# Revit family: Турникет тумбовый PERCo_TTD-03.2
name_source: partatom
category: Mechanical Equipment
units: mm (PartAtom-declared; Revit-internal decimal feet)

## family parameters
Always vertical = No
Classification = None
Cut with Voids When Loaded = No
Part Type = Normal
Room Calculation Point = No
Round Connector Dimension = Use Diameter
Shared = No
Work Plane-Based = No

## types (2) — shared parameters
Built-in reader = not provided
Card capture reader capacity = not provided
Current = 1 A
Dimensions = 980 х 664 x 1010 mm
Electrical connection = 220 V
IP Code = IP41
Lid = Stainless steel
Manufacturer = PERCo
Maximum dimensions of ACS controller = max. 250 ×175 ×40 mm
Maximum dimensions of installed readers = max. 100×130×28 mm
Number = 1
Operating temperature = from +1°С to +50°С
Passageway width = 500 mm
Plank length = 511 mm
Rated power = 9 W
Throughput rate = 30 persons/min
URL = https://www.perco.com
Unit of measurement = pcs
Voltage = 12 V
Weight = max. 60 kg

## per-type parameters (varying)
| type | Frame | Full name | Material | Name |
| TTD-03.2G | Powder coated steel | TTD-03.2G Electromechanical Box Tripod Turnstile for indoor application | Housing ─ powder-coated steel. Top cover ─ stainless steel or radio-transparent artificial stone. Barrier arms ─ stainless steel. | TTD-03.2G Box tripod turnstile |
| TTD-03.2S | Stainless steel | TTD-03.2S Electromechanical Box Tripod Turnstile for indoor application | Housing ─ high-quality stainless steel. Top cover ─ stainless steel or radio-transparent artificial stone. Barrier arms ─ stainless steel. | TTD-03.2S Box tripod turnstile |
